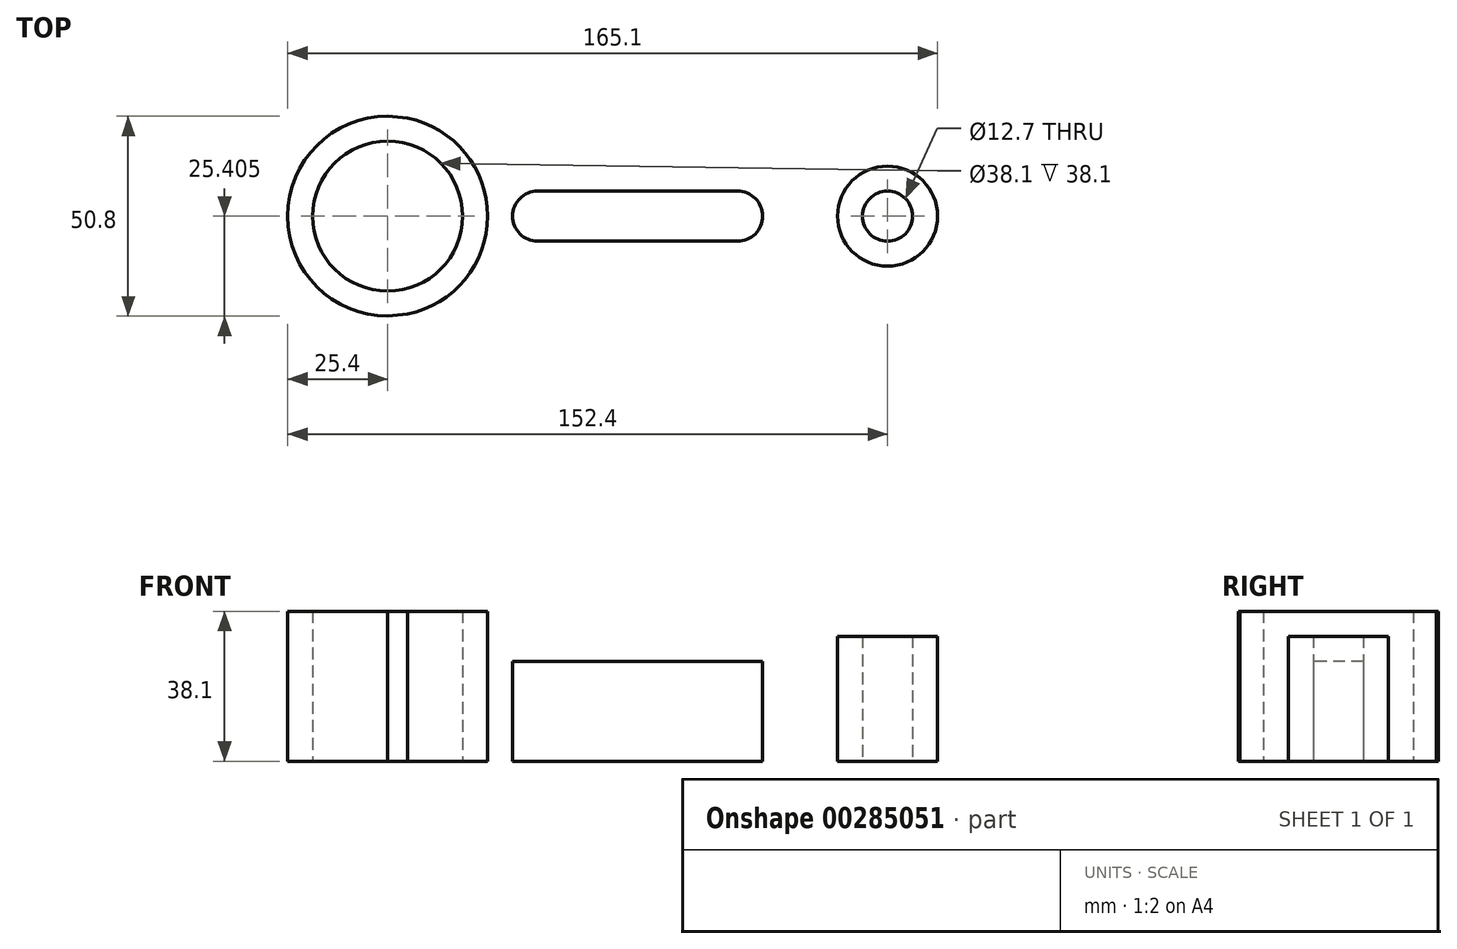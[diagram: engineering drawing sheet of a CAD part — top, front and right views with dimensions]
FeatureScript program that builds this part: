
annotation { "Feature Type Name" : "Feature", "Feature Type Description" : "" }
export const myFeature = defineFeature(function(context is Context, id is Id, definition is map)
    precondition{}
    {
        {
            var Q0;
            Q0=qCreatedBy(makeId("Top.planeOp"),FACE);
            var sketch = newSketch(context, id + "F0", { "sketchPlane" : qUnion([Q0])});
            skCircle(sketch, "E0", {"center": v(-112.3, 7.45) * mm, "radius": 19.05 * mm});
            skCircle(sketch, "E1", {"center": v(-112.3, 7.45) * mm, "radius": 25.4 * mm});
            skCircle(sketch, "E2", {"center": v(14.7, 7.45) * mm, "radius": 6.35 * mm});
            skCircle(sketch, "E3", {"center": v(14.7, 7.45) * mm, "radius": 12.7 * mm});
            skLineSegment(sketch, "E4", {"start": v(-112.3, 32.85) * mm, "end": v(14.7, 20.15) * mm});
            skLineSegment(sketch, "E5", {"start": v(-112.3, -17.95) * mm, "end": v(14.7, -5.25) * mm});
            skArc(sketch, "E6", {"start": v(-23.4, 13.8) * mm, "mid": v(-17.04, 7.45) * mm, "end": v(-23.4, 1.1) * mm});
            skArc(sketch, "E7", {"start": v(-74.2, 13.8) * mm, "mid": v(-80.54, 7.45) * mm, "end": v(-74.2, 1.1) * mm});
            skLineSegment(sketch, "E8", {"start": v(-74.2, 13.8) * mm, "end": v(-23.4, 13.8) * mm});
            skLineSegment(sketch, "E9", {"start": v(-74.2, 1.1) * mm, "end": v(-23.4, 1.1) * mm});
            skSolve(sketch);
        }
        {
            var Q0;
            Q0=makeQuery(id+"F0.imprint","IMPRINT",FACE,{"disambiguationData":[TD([[makeQuery(id+"F0.imprint","IMPRINT",EDGE,{"derivedFrom":sQuery(id+"F0.wireOp",EDGE,"E0")}),-1.0]])]});
            extrude(context, id + "F1", {"entities" : qUnion([Q0]), "depth" : 38.1 * mm});
        }
        {
            var Q0;
            Q0=makeQuery(id+"F0.imprint","IMPRINT",FACE,{"disambiguationData":[TD([[makeQuery(id+"F0.imprint","IMPRINT",EDGE,{"derivedFrom":sQuery(id+"F0.wireOp",EDGE,"E6")}),1.0]])]});
            extrude(context, id + "F2", {"entities" : qUnion([Q0]), "operationType" : NewBodyOperationType.ADD, "depth" : 25.4 * mm});
        }
        {
            var Q0;
            Q0=makeQuery(id+"F0.imprint","IMPRINT",FACE,{"disambiguationData":[TD([[makeQuery(id+"F0.imprint","IMPRINT",EDGE,{"derivedFrom":sQuery(id+"F0.wireOp",EDGE,"E2")}),-1.0]])]});
            extrude(context, id + "F3", {"entities" : qUnion([Q0]), "operationType" : NewBodyOperationType.ADD, "depth" : 31.75 * mm});
        }
    });
